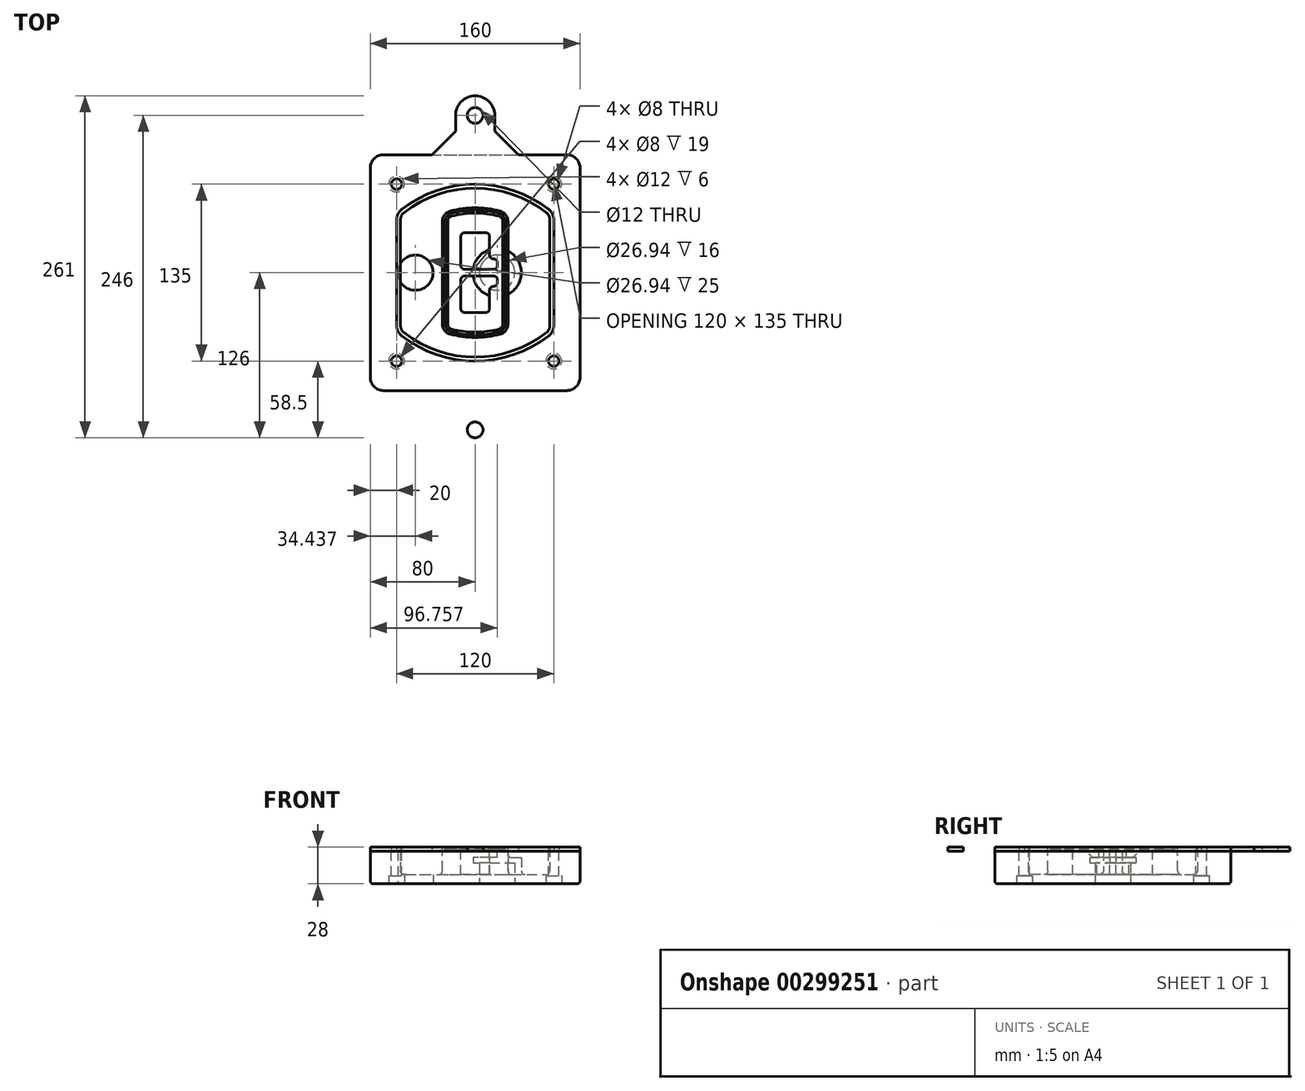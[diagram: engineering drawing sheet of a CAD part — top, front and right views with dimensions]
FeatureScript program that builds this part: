
annotation { "Feature Type Name" : "Feature", "Feature Type Description" : "" }
export const myFeature = defineFeature(function(context is Context, id is Id, definition is map)
    precondition{}
    {
        {
            var Q0;
            Q0=qCreatedBy(makeId("Top.planeOp"),FACE);
            var sketch = newSketch(context, id + "F0", { "sketchPlane" : qUnion([Q0])});
            skPoint(sketch, "E0.rect.middle", {"position": v(0, 0) * mm});
            skLineSegment(sketch, "E1.bottom", {"start": v(-70, -90) * mm, "end": v(70, -90) * mm});
            skLineSegment(sketch, "E1.top", {"start": v(-70, 90) * mm, "end": v(70, 90) * mm});
            skLineSegment(sketch, "E1.left", {"start": v(-80, -80) * mm, "end": v(-80, 80) * mm});
            skLineSegment(sketch, "E1.right", {"start": v(80, -80) * mm, "end": v(80, 80) * mm});
            skLineSegment(sketch, "E2", {"start": v(-80, 90) * mm, "end": v(80, -90) * mm, "construction": true});
            skLineSegment(sketch, "E3", {"start": v(80, 90) * mm, "end": v(-80, -90) * mm, "construction": true});
            skCircle(sketch, "E4", {"center": v(-60, 67.5) * mm, "radius": 4 * mm});
            skCircle(sketch, "E5", {"center": v(60, 67.5) * mm, "radius": 4 * mm});
            skCircle(sketch, "E6", {"center": v(60, -67.5) * mm, "radius": 4 * mm});
            skCircle(sketch, "E7", {"center": v(-60, -67.5) * mm, "radius": 4 * mm});
            skLineSegment(sketch, "E8", {"start": v(-60, 67.5) * mm, "end": v(60, 67.5) * mm, "construction": true});
            skLineSegment(sketch, "E9", {"start": v(60, 67.5) * mm, "end": v(60, -67.5) * mm, "construction": true});
            skLineSegment(sketch, "E10", {"start": v(60, -67.5) * mm, "end": v(-60, -67.5) * mm, "construction": true});
            skLineSegment(sketch, "E11", {"start": v(-60, -67.5) * mm, "end": v(-60, 67.5) * mm, "construction": true});
            skLineSegment(sketch, "E12", {"start": v(-60, 40.3) * mm, "end": v(-60, -40.3) * mm});
            skLineSegment(sketch, "E13", {"start": v(60, 40.3) * mm, "end": v(60, -40.3) * mm});
            skArc(sketch, "E14", {"start": v(56.15, 48.18) * mm, "mid": v(0, 67.5) * mm, "end": v(-56.15, 48.18) * mm});
            skArc(sketch, "E15", {"start": v(-56.15, -48.18) * mm, "mid": v(0, -67.5) * mm, "end": v(56.15, -48.18) * mm});
            skLineSegment(sketch, "E16", {"start": v(-60, 0) * mm, "end": v(60, 0) * mm, "construction": true});
            skPoint(sketch, "E17.visualSharp", {"position": v(-60, -45) * mm});
            skArc(sketch, "E17.filletArc", {"start": v(-60, -40.3) * mm, "mid": v(-58.99, -44.68) * mm, "end": v(-56.15, -48.18) * mm});
            skPoint(sketch, "E18.visualSharp", {"position": v(-60, 45) * mm});
            skArc(sketch, "E18.filletArc", {"start": v(-56.15, 48.18) * mm, "mid": v(-58.99, 44.68) * mm, "end": v(-60, 40.3) * mm});
            skPoint(sketch, "E19.visualSharp", {"position": v(60, 45) * mm});
            skArc(sketch, "E19.filletArc", {"start": v(60, 40.3) * mm, "mid": v(58.99, 44.68) * mm, "end": v(56.15, 48.18) * mm});
            skPoint(sketch, "E20.visualSharp", {"position": v(60, -45) * mm});
            skArc(sketch, "E20.filletArc", {"start": v(56.15, -48.18) * mm, "mid": v(58.99, -44.68) * mm, "end": v(60, -40.3) * mm});
            skPoint(sketch, "E21.visualSharp", {"position": v(-80, 90) * mm});
            skArc(sketch, "E21.filletArc", {"start": v(-70, 90) * mm, "mid": v(-77.07, 87.07) * mm, "end": v(-80, 80) * mm});
            skPoint(sketch, "E22.visualSharp", {"position": v(80, 90) * mm});
            skArc(sketch, "E22.filletArc", {"start": v(80, 80) * mm, "mid": v(77.07, 87.07) * mm, "end": v(70, 90) * mm});
            skPoint(sketch, "E23.visualSharp", {"position": v(80, -90) * mm});
            skArc(sketch, "E23.filletArc", {"start": v(70, -90) * mm, "mid": v(77.07, -87.07) * mm, "end": v(80, -80) * mm});
            skPoint(sketch, "E24.visualSharp", {"position": v(-80, -90) * mm});
            skArc(sketch, "E24.filletArc", {"start": v(-80, -80) * mm, "mid": v(-77.07, -87.07) * mm, "end": v(-70, -90) * mm});
            skArc(sketch, "E25.0", {"start": v(57, 40.3) * mm, "mid": v(56.3, 43.36) * mm, "end": v(54.3, 45.81) * mm});
            skLineSegment(sketch, "E25.1", {"start": v(57, 40.3) * mm, "end": v(57, -40.3) * mm});
            skArc(sketch, "E25.2", {"start": v(54.3, -45.81) * mm, "mid": v(56.3, -43.36) * mm, "end": v(57, -40.3) * mm});
            skArc(sketch, "E25.3", {"start": v(-54.3, -45.81) * mm, "mid": v(0, -64.5) * mm, "end": v(54.3, -45.81) * mm});
            skArc(sketch, "E25.4", {"start": v(-57, -40.3) * mm, "mid": v(-56.3, -43.36) * mm, "end": v(-54.3, -45.81) * mm});
            skArc(sketch, "E25.5", {"start": v(54.3, 45.81) * mm, "mid": v(0, 64.5) * mm, "end": v(-54.3, 45.81) * mm});
            skLineSegment(sketch, "E25.6", {"start": v(-57, 40.3) * mm, "end": v(-57, -40.3) * mm});
            skArc(sketch, "E25.7", {"start": v(-54.3, 45.81) * mm, "mid": v(-56.3, 43.36) * mm, "end": v(-57, 40.3) * mm});
            skArc(sketch, "E26.0", {"start": v(-58.62, 51.33) * mm, "mid": v(-62.58, 46.43) * mm, "end": v(-64, 40.3) * mm});
            skArc(sketch, "E26.1", {"start": v(58.62, 51.33) * mm, "mid": v(0, 71.5) * mm, "end": v(-58.62, 51.33) * mm});
            skArc(sketch, "E26.2", {"start": v(64, 40.3) * mm, "mid": v(62.58, 46.43) * mm, "end": v(58.62, 51.33) * mm});
            skLineSegment(sketch, "E26.3", {"start": v(64, 40.3) * mm, "end": v(64, -40.3) * mm});
            skArc(sketch, "E26.4", {"start": v(58.62, -51.33) * mm, "mid": v(62.58, -46.43) * mm, "end": v(64, -40.3) * mm});
            skLineSegment(sketch, "E26.5", {"start": v(-64, 40.3) * mm, "end": v(-64, -40.3) * mm});
            skArc(sketch, "E26.6", {"start": v(-58.62, -51.33) * mm, "mid": v(0, -71.5) * mm, "end": v(58.62, -51.33) * mm});
            skArc(sketch, "E26.7", {"start": v(-64, -40.3) * mm, "mid": v(-62.58, -46.43) * mm, "end": v(-58.62, -51.33) * mm});
            skSolve(sketch);
        }
        {
            var Q0;
            Q0=makeQuery(id+"F0.imprint","IMPRINT",FACE,{"disambiguationData":[TD([[makeQuery(id+"F0.imprint","IMPRINT",EDGE,{"derivedFrom":sQuery(id+"F0.wireOp",EDGE,"E1.bottom")}),1.0]])]});
            var Q1;
            Q1=makeQuery(id+"F0.imprint","IMPRINT",FACE,{"disambiguationData":[TD([[makeQuery(id+"F0.imprint","IMPRINT",EDGE,{"derivedFrom":sQuery(id+"F0.wireOp",EDGE,"E12")}),1.0]])]});
            var Q2;
            Q2=makeQuery(id+"F0.imprint","IMPRINT",FACE,{"disambiguationData":[TD([[makeQuery(id+"F0.imprint","IMPRINT",EDGE,{"derivedFrom":sQuery(id+"F0.wireOp",EDGE,"E25.0")}),1.0]])]});
            var Q3;
            Q3=makeQuery(id+"F0.imprint","IMPRINT",FACE,{"disambiguationData":[TD([[makeQuery(id+"F0.imprint","IMPRINT",EDGE,{"derivedFrom":sQuery(id+"F0.wireOp",EDGE,"E12")}),-1.0]])]});
            extrude(context, id + "F1", {"entities" : qUnion([Q0, Q1, Q2, Q3]), "oppositeDirection" : true, "depth" : 25 * mm});
        }
        {
            var Q0;
            Q0=makeQuery(id+"F0.imprint","IMPRINT",FACE,{"disambiguationData":[TD([[makeQuery(id+"F0.imprint","IMPRINT",EDGE,{"derivedFrom":sQuery(id+"F0.wireOp",EDGE,"E12")}),1.0]])]});
            extrude(context, id + "F2", {"entities" : qUnion([Q0]), "operationType" : NewBodyOperationType.ADD, "depth" : 3 * mm});
        }
        {
            var Q0;
            Q0=makeQuery(id+"F0.imprint","IMPRINT",FACE,{"disambiguationData":[TD([[makeQuery(id+"F0.imprint","IMPRINT",EDGE,{"derivedFrom":sQuery(id+"F0.wireOp",EDGE,"E25.0")}),1.0]])]});
            extrude(context, id + "F3", {"entities" : qUnion([Q0]), "operationType" : NewBodyOperationType.REMOVE, "oppositeDirection" : true, "depth" : 18 * mm});
        }
        {
            var Q0;
            Q0=makeQuery(id+"F2.opExtrude","CAP_FACE",FACE,{"disambiguationData":[OSD([sQuery(id+"F0.wireOp",EDGE,"E12"),sQuery(id+"F0.wireOp",EDGE,"E13"),sQuery(id+"F0.wireOp",EDGE,"E14"),sQuery(id+"F0.wireOp",EDGE,"E15"),sQuery(id+"F0.wireOp",EDGE,"E17.filletArc"),sQuery(id+"F0.wireOp",EDGE,"E18.filletArc"),sQuery(id+"F0.wireOp",EDGE,"E19.filletArc"),sQuery(id+"F0.wireOp",EDGE,"E20.filletArc"),sQuery(id+"F0.wireOp",EDGE,"E25.0"),sQuery(id+"F0.wireOp",EDGE,"E25.1"),sQuery(id+"F0.wireOp",EDGE,"E25.2"),sQuery(id+"F0.wireOp",EDGE,"E25.3"),sQuery(id+"F0.wireOp",EDGE,"E25.4"),sQuery(id+"F0.wireOp",EDGE,"E25.5"),sQuery(id+"F0.wireOp",EDGE,"E25.6"),sQuery(id+"F0.wireOp",EDGE,"E25.7")])],"isStart":false});
            var sketch = newSketch(context, id + "F4", { "sketchPlane" : qUnion([Q0])});
            skArc(sketch, "E27.0", {"start": v(-19.08, -46.97) * mm, "mid": v(0, -49.5) * mm, "end": v(19.08, -46.97) * mm});
            skArc(sketch, "E28.0", {"start": v(19.08, 46.97) * mm, "mid": v(0, 49.5) * mm, "end": v(-19.08, 46.97) * mm});
            skLineSegment(sketch, "E29", {"start": v(-25, 39.25) * mm, "end": v(-25, -39.25) * mm});
            skLineSegment(sketch, "E30", {"start": v(25, 39.25) * mm, "end": v(25, -39.25) * mm});
            skLineSegment(sketch, "E31", {"start": v(-25, 45.1) * mm, "end": v(25, 45.1) * mm, "construction": true});
            skLineSegment(sketch, "E32", {"start": v(-25, -45.1) * mm, "end": v(25, -45.1) * mm, "construction": true});
            skPoint(sketch, "E33.visualSharp", {"position": v(-25, 45.1) * mm});
            skArc(sketch, "E33.filletArc", {"start": v(-19.08, 46.97) * mm, "mid": v(-23.35, 44.11) * mm, "end": v(-25, 39.25) * mm});
            skPoint(sketch, "E34.visualSharp", {"position": v(25, 45.1) * mm});
            skArc(sketch, "E34.filletArc", {"start": v(25, 39.25) * mm, "mid": v(23.35, 44.11) * mm, "end": v(19.08, 46.97) * mm});
            skPoint(sketch, "E35.visualSharp", {"position": v(25, -45.1) * mm});
            skArc(sketch, "E35.filletArc", {"start": v(19.08, -46.97) * mm, "mid": v(23.35, -44.11) * mm, "end": v(25, -39.25) * mm});
            skPoint(sketch, "E36.visualSharp", {"position": v(-25, -45.1) * mm});
            skArc(sketch, "E36.filletArc", {"start": v(-25, -39.25) * mm, "mid": v(-23.35, -44.11) * mm, "end": v(-19.08, -46.97) * mm});
            skArc(sketch, "E37.0", {"start": v(54.3, 45.81) * mm, "mid": v(0, 64.5) * mm, "end": v(-54.3, 45.81) * mm});
            skArc(sketch, "E37.1", {"start": v(-54.3, 45.81) * mm, "mid": v(-56.3, 43.36) * mm, "end": v(-57, 40.3) * mm});
            skLineSegment(sketch, "E37.2", {"start": v(-57, 40.3) * mm, "end": v(-57, -40.3) * mm});
            skArc(sketch, "E37.3", {"start": v(-57, -40.3) * mm, "mid": v(-56.3, -43.36) * mm, "end": v(-54.3, -45.81) * mm});
            skArc(sketch, "E37.4", {"start": v(-54.3, -45.81) * mm, "mid": v(0, -64.5) * mm, "end": v(54.3, -45.81) * mm});
            skArc(sketch, "E37.5", {"start": v(54.3, -45.81) * mm, "mid": v(56.3, -43.36) * mm, "end": v(57, -40.3) * mm});
            skLineSegment(sketch, "E37.6", {"start": v(57, 40.3) * mm, "end": v(57, -40.3) * mm});
            skArc(sketch, "E37.7", {"start": v(57, 40.3) * mm, "mid": v(56.3, 43.36) * mm, "end": v(54.3, 45.81) * mm});
            skLineSegment(sketch, "E38.0", {"start": v(23, 39.25) * mm, "end": v(23, -39.25) * mm});
            skArc(sketch, "E38.1", {"start": v(18.56, -45.04) * mm, "mid": v(21.76, -42.9) * mm, "end": v(23, -39.25) * mm});
            skArc(sketch, "E38.2", {"start": v(-18.56, -45.04) * mm, "mid": v(0, -47.5) * mm, "end": v(18.56, -45.04) * mm});
            skArc(sketch, "E38.3", {"start": v(-23, -39.25) * mm, "mid": v(-21.76, -42.9) * mm, "end": v(-18.56, -45.04) * mm});
            skLineSegment(sketch, "E38.4", {"start": v(-23, 39.25) * mm, "end": v(-23, -39.25) * mm});
            skArc(sketch, "E38.5", {"start": v(23, 39.25) * mm, "mid": v(21.76, 42.9) * mm, "end": v(18.56, 45.04) * mm});
            skArc(sketch, "E38.6", {"start": v(-18.56, 45.04) * mm, "mid": v(-21.76, 42.9) * mm, "end": v(-23, 39.25) * mm});
            skArc(sketch, "E38.7", {"start": v(18.56, 45.04) * mm, "mid": v(0, 47.5) * mm, "end": v(-18.56, 45.04) * mm});
            skArc(sketch, "E39.0", {"start": v(21, 39.25) * mm, "mid": v(20.18, 41.68) * mm, "end": v(18.04, 43.1) * mm});
            skLineSegment(sketch, "E39.1", {"start": v(21, 39.25) * mm, "end": v(21, -39.25) * mm});
            skArc(sketch, "E39.2", {"start": v(18.04, -43.1) * mm, "mid": v(20.18, -41.68) * mm, "end": v(21, -39.25) * mm});
            skArc(sketch, "E39.3", {"start": v(-18.04, -43.1) * mm, "mid": v(0, -45.5) * mm, "end": v(18.04, -43.1) * mm});
            skArc(sketch, "E39.4", {"start": v(-21, -39.25) * mm, "mid": v(-20.18, -41.68) * mm, "end": v(-18.04, -43.1) * mm});
            skArc(sketch, "E39.5", {"start": v(18.04, 43.1) * mm, "mid": v(0, 45.5) * mm, "end": v(-18.04, 43.1) * mm});
            skLineSegment(sketch, "E39.6", {"start": v(-21, 39.25) * mm, "end": v(-21, -39.25) * mm});
            skArc(sketch, "E39.7", {"start": v(-18.04, 43.1) * mm, "mid": v(-20.18, 41.68) * mm, "end": v(-21, 39.25) * mm});
            skLineSegment(sketch, "E40", {"start": v(-25, 0) * mm, "end": v(25, 0) * mm, "construction": true});
            skLineSegment(sketch, "E41", {"start": v(-11, 5.5) * mm, "end": v(-11, 27.5) * mm});
            skLineSegment(sketch, "E42", {"start": v(-8, 30.5) * mm, "end": v(8, 30.5) * mm});
            skLineSegment(sketch, "E43", {"start": v(11, 27.5) * mm, "end": v(11, 13.5) * mm});
            skLineSegment(sketch, "E44", {"start": v(14, 10.5) * mm, "end": v(14, 10.5) * mm});
            skLineSegment(sketch, "E45", {"start": v(17, 7.5) * mm, "end": v(17, 5.5) * mm});
            skLineSegment(sketch, "E46", {"start": v(14, 2.5) * mm, "end": v(-8, 2.5) * mm});
            skPoint(sketch, "E47.visualSharp", {"position": v(-11, 30.5) * mm});
            skArc(sketch, "E47.filletArc", {"start": v(-8, 30.5) * mm, "mid": v(-10.12, 29.62) * mm, "end": v(-11, 27.5) * mm});
            skPoint(sketch, "E48.visualSharp", {"position": v(11, 30.5) * mm});
            skArc(sketch, "E48.filletArc", {"start": v(11, 27.5) * mm, "mid": v(10.12, 29.62) * mm, "end": v(8, 30.5) * mm});
            skPoint(sketch, "E49.visualSharp", {"position": v(11, 10.5) * mm});
            skArc(sketch, "E49.filletArc", {"start": v(11, 13.5) * mm, "mid": v(11.88, 11.38) * mm, "end": v(14, 10.5) * mm});
            skPoint(sketch, "E50.visualSharp", {"position": v(17, 10.5) * mm});
            skArc(sketch, "E50.filletArc", {"start": v(17, 7.5) * mm, "mid": v(16.12, 9.62) * mm, "end": v(14, 10.5) * mm});
            skPoint(sketch, "E51.visualSharp", {"position": v(17, 2.5) * mm});
            skArc(sketch, "E51.filletArc", {"start": v(14, 2.5) * mm, "mid": v(16.12, 3.38) * mm, "end": v(17, 5.5) * mm});
            skPoint(sketch, "E52.visualSharp", {"position": v(-11, 2.5) * mm});
            skArc(sketch, "E52.filletArc", {"start": v(-11, 5.5) * mm, "mid": v(-10.12, 3.38) * mm, "end": v(-8, 2.5) * mm});
            skLineSegment(sketch, "E53.0.MirrorCS", {"start": v(14, -2.5) * mm, "end": v(-8, -2.5) * mm});
            skArc(sketch, "E54.0.MirrorCS", {"start": v(-11, -5.5) * mm, "mid": v(-10.12, -3.38) * mm, "end": v(-8, -2.5) * mm});
            skLineSegment(sketch, "E55.0.MirrorCS", {"start": v(-11, -5.5) * mm, "end": v(-11, -27.5) * mm});
            skArc(sketch, "E56.0.MirrorCS", {"start": v(-8, -30.5) * mm, "mid": v(-10.12, -29.62) * mm, "end": v(-11, -27.5) * mm});
            skLineSegment(sketch, "E57.0.MirrorCS", {"start": v(-8, -30.5) * mm, "end": v(8, -30.5) * mm});
            skArc(sketch, "E58.0.MirrorCS", {"start": v(11, -27.5) * mm, "mid": v(10.12, -29.62) * mm, "end": v(8, -30.5) * mm});
            skLineSegment(sketch, "E59.0.MirrorCS", {"start": v(11, -27.5) * mm, "end": v(11, -13.5) * mm});
            skArc(sketch, "E60.0.MirrorCS", {"start": v(11, -13.5) * mm, "mid": v(11.88, -11.38) * mm, "end": v(14, -10.5) * mm});
            skArc(sketch, "E61.0.MirrorCS", {"start": v(17, -7.5) * mm, "mid": v(16.12, -9.62) * mm, "end": v(14, -10.5) * mm});
            skLineSegment(sketch, "E62.0.MirrorCS", {"start": v(17, -7.5) * mm, "end": v(17, -5.5) * mm});
            skArc(sketch, "E63.0.MirrorCS", {"start": v(14, -2.5) * mm, "mid": v(16.12, -3.38) * mm, "end": v(17, -5.5) * mm});
            skSolve(sketch);
        }
        {
            var Q0;
            Q0=makeQuery(id+"F4.imprint","IMPRINT",FACE,{"disambiguationData":[TD([[makeQuery(id+"F4.imprint","IMPRINT",EDGE,{"derivedFrom":sQuery(id+"F4.wireOp",EDGE,"E27.0")}),1.0]])]});
            var Q1;
            Q1=makeQuery(id+"F4.imprint","IMPRINT",FACE,{"disambiguationData":[TD([[makeQuery(id+"F4.imprint","IMPRINT",EDGE,{"derivedFrom":sQuery(id+"F4.wireOp",EDGE,"E38.0")}),-1.0]])]});
            var Q2;
            Q2=makeQuery(id+"F4.imprint","IMPRINT",FACE,{"disambiguationData":[TD([[makeQuery(id+"F4.imprint","IMPRINT",EDGE,{"derivedFrom":sQuery(id+"F4.wireOp",EDGE,"E39.0")}),1.0]])]});
            extrude(context, id + "F5", {"entities" : qUnion([Q0, Q1, Q2]), "operationType" : NewBodyOperationType.ADD, "endBound" : BoundingType.UP_TO_NEXT, "oppositeDirection" : true, "depth" : 25 * mm});
        }
        {
            var Q0;
            Q0=makeQuery(id+"F4.imprint","IMPRINT",FACE,{"disambiguationData":[TD([[makeQuery(id+"F4.imprint","IMPRINT",EDGE,{"derivedFrom":sQuery(id+"F4.wireOp",EDGE,"E38.0")}),-1.0]])]});
            extrude(context, id + "F6", {"entities" : qUnion([Q0]), "operationType" : NewBodyOperationType.REMOVE, "oppositeDirection" : true, "depth" : 2 * mm});
        }
        {
            var Q0;
            Q0=makeQuery(id+"F1.opExtrude","CAP_FACE",FACE,{"disambiguationData":[OSD([sQuery(id+"F0.wireOp",EDGE,"E1.bottom"),sQuery(id+"F0.wireOp",EDGE,"E1.top"),sQuery(id+"F0.wireOp",EDGE,"E1.left"),sQuery(id+"F0.wireOp",EDGE,"E1.right"),sQuery(id+"F0.wireOp",EDGE,"E4"),sQuery(id+"F0.wireOp",EDGE,"E5"),sQuery(id+"F0.wireOp",EDGE,"E6"),sQuery(id+"F0.wireOp",EDGE,"E7"),sQuery(id+"F0.wireOp",EDGE,"E21.filletArc"),sQuery(id+"F0.wireOp",EDGE,"E22.filletArc"),sQuery(id+"F0.wireOp",EDGE,"E23.filletArc"),sQuery(id+"F0.wireOp",EDGE,"E24.filletArc")])],"isStart":false});
            var sketch = newSketch(context, id + "F7", { "sketchPlane" : qUnion([Q0])});
            skCircle(sketch, "E64", {"center": v(16.76, 0) * mm, "radius": 13.47 * mm});
            skCircle(sketch, "E65", {"center": v(-45.56, 0) * mm, "radius": 13.47 * mm});
            skLineSegment(sketch, "E66", {"start": v(80, 0) * mm, "end": v(-80, 0) * mm});
            skCircle(sketch, "E67", {"center": v(16.76, 0) * mm, "radius": 18.47 * mm});
            skCircle(sketch, "E68", {"center": v(60, -67.5) * mm, "radius": 6 * mm});
            skCircle(sketch, "E69", {"center": v(-60, -67.5) * mm, "radius": 6 * mm});
            skCircle(sketch, "E70", {"center": v(-60, 67.5) * mm, "radius": 6 * mm});
            skCircle(sketch, "E71", {"center": v(60, 67.5) * mm, "radius": 6 * mm});
            skSolve(sketch);
        }
        {
            var Q0;
            {var subQ1=sQuery(id+"F7.wireOp",EDGE,"E66");var subQ4=sQuery(id+"F7.wireOp",EDGE,"E64");var subQ6=makeQuery(id+"F7.imprint","INTERSECT",VERTEX,{"disambiguationData":[OD(0.0)],"derivedFrom":[subQ4,subQ1]});Q0=makeQuery(id+"F7.imprint","IMPRINT",FACE,{"disambiguationData":[TD([[makeQuery(id+"F7.imprint","IMPRINT",EDGE,{"disambiguationData":[TD([[subQ6,-1.0]])],"derivedFrom":subQ4}),-1.0]])]});}
            var Q1;
            {var subQ0=sQuery(id+"F7.wireOp",EDGE,"E66");var subQ1=sQuery(id+"F7.wireOp",EDGE,"E64");var subQ3=makeQuery(id+"F7.imprint","INTERSECT",VERTEX,{"disambiguationData":[OD(0.0)],"derivedFrom":[subQ1,subQ0]});Q1=makeQuery(id+"F7.imprint","IMPRINT",FACE,{"disambiguationData":[TD([[makeQuery(id+"F7.imprint","IMPRINT",EDGE,{"disambiguationData":[TD([[subQ3,-1.0]])],"derivedFrom":subQ1}),1.0]])]});}
            var Q2;
            {var subQ0=sQuery(id+"F7.wireOp",EDGE,"E66");var subQ1=sQuery(id+"F7.wireOp",EDGE,"E64");var subQ3=makeQuery(id+"F7.imprint","INTERSECT",VERTEX,{"disambiguationData":[OD(0.0)],"derivedFrom":[subQ1,subQ0]});Q2=makeQuery(id+"F7.imprint","IMPRINT",FACE,{"disambiguationData":[TD([[makeQuery(id+"F7.imprint","IMPRINT",EDGE,{"disambiguationData":[TD([[subQ3,1.0]])],"derivedFrom":subQ1}),1.0]])]});}
            var Q3;
            {var subQ1=sQuery(id+"F7.wireOp",EDGE,"E66");var subQ4=sQuery(id+"F7.wireOp",EDGE,"E64");var subQ6=makeQuery(id+"F7.imprint","INTERSECT",VERTEX,{"disambiguationData":[OD(0.0)],"derivedFrom":[subQ4,subQ1]});Q3=makeQuery(id+"F7.imprint","IMPRINT",FACE,{"disambiguationData":[TD([[makeQuery(id+"F7.imprint","IMPRINT",EDGE,{"disambiguationData":[TD([[subQ6,1.0]])],"derivedFrom":subQ4}),-1.0]])]});}
            extrude(context, id + "F8", {"entities" : qUnion([Q0, Q1, Q2, Q3]), "operationType" : NewBodyOperationType.ADD, "oppositeDirection" : true, "depth" : 20 * mm});
        }
        {
            var Q0;
            {var subQ0=sQuery(id+"F7.wireOp",EDGE,"E66");var subQ1=sQuery(id+"F7.wireOp",EDGE,"E64");var subQ3=makeQuery(id+"F7.imprint","INTERSECT",VERTEX,{"disambiguationData":[OD(0.0)],"derivedFrom":[subQ1,subQ0]});Q0=makeQuery(id+"F7.imprint","IMPRINT",FACE,{"disambiguationData":[TD([[makeQuery(id+"F7.imprint","IMPRINT",EDGE,{"disambiguationData":[TD([[subQ3,-1.0]])],"derivedFrom":subQ1}),1.0]])]});}
            var Q1;
            {var subQ0=sQuery(id+"F7.wireOp",EDGE,"E66");var subQ1=sQuery(id+"F7.wireOp",EDGE,"E64");var subQ3=makeQuery(id+"F7.imprint","INTERSECT",VERTEX,{"disambiguationData":[OD(0.0)],"derivedFrom":[subQ1,subQ0]});Q1=makeQuery(id+"F7.imprint","IMPRINT",FACE,{"disambiguationData":[TD([[makeQuery(id+"F7.imprint","IMPRINT",EDGE,{"disambiguationData":[TD([[subQ3,1.0]])],"derivedFrom":subQ1}),1.0]])]});}
            extrude(context, id + "F9", {"entities" : qUnion([Q0, Q1]), "operationType" : NewBodyOperationType.REMOVE, "oppositeDirection" : true, "depth" : 16 * mm});
        }
        {
            var Q0;
            {var subQ0=sQuery(id+"F7.wireOp",EDGE,"E66");var subQ1=sQuery(id+"F7.wireOp",EDGE,"E65");var subQ3=makeQuery(id+"F7.imprint","INTERSECT",VERTEX,{"disambiguationData":[OD(0.0)],"derivedFrom":[subQ1,subQ0]});Q0=makeQuery(id+"F7.imprint","IMPRINT",FACE,{"disambiguationData":[TD([[makeQuery(id+"F7.imprint","IMPRINT",EDGE,{"disambiguationData":[TD([[subQ3,-1.0]])],"derivedFrom":subQ1}),1.0]])]});}
            var Q1;
            {var subQ0=sQuery(id+"F7.wireOp",EDGE,"E66");var subQ1=sQuery(id+"F7.wireOp",EDGE,"E65");var subQ3=makeQuery(id+"F7.imprint","INTERSECT",VERTEX,{"disambiguationData":[OD(0.0)],"derivedFrom":[subQ1,subQ0]});Q1=makeQuery(id+"F7.imprint","IMPRINT",FACE,{"disambiguationData":[TD([[makeQuery(id+"F7.imprint","IMPRINT",EDGE,{"disambiguationData":[TD([[subQ3,1.0]])],"derivedFrom":subQ1}),1.0]])]});}
            extrude(context, id + "F10", {"entities" : qUnion([Q0, Q1]), "operationType" : NewBodyOperationType.REMOVE, "oppositeDirection" : true, "depth" : 25 * mm});
        }
        {
            var Q0;
            Q0=makeQuery(id+"F7.imprint","IMPRINT",FACE,{"disambiguationData":[TD([[makeQuery(id+"F7.imprint","IMPRINT",EDGE,{"derivedFrom":sQuery(id+"F7.wireOp",EDGE,"E68")}),1.0]])]});
            var Q1;
            Q1=makeQuery(id+"F7.imprint","IMPRINT",FACE,{"disambiguationData":[TD([[makeQuery(id+"F7.imprint","IMPRINT",EDGE,{"derivedFrom":makeQuery(id+"F1.opExtrude","CAP_EDGE",EDGE,{"disambiguationData":[OSD([sQuery(id+"F0.wireOp",EDGE,"E5")])],"isStart":false})}),-1.0]])]});
            var Q2;
            Q2=makeQuery(id+"F7.imprint","IMPRINT",FACE,{"disambiguationData":[TD([[makeQuery(id+"F7.imprint","IMPRINT",EDGE,{"derivedFrom":sQuery(id+"F7.wireOp",EDGE,"E69")}),1.0]])]});
            var Q3;
            Q3=makeQuery(id+"F7.imprint","IMPRINT",FACE,{"disambiguationData":[TD([[makeQuery(id+"F7.imprint","IMPRINT",EDGE,{"derivedFrom":makeQuery(id+"F1.opExtrude","CAP_EDGE",EDGE,{"disambiguationData":[OSD([sQuery(id+"F0.wireOp",EDGE,"E4")])],"isStart":false})}),-1.0]])]});
            var Q4;
            Q4=makeQuery(id+"F7.imprint","IMPRINT",FACE,{"disambiguationData":[TD([[makeQuery(id+"F7.imprint","IMPRINT",EDGE,{"derivedFrom":sQuery(id+"F7.wireOp",EDGE,"E70")}),1.0]])]});
            var Q5;
            Q5=makeQuery(id+"F7.imprint","IMPRINT",FACE,{"disambiguationData":[TD([[makeQuery(id+"F7.imprint","IMPRINT",EDGE,{"derivedFrom":makeQuery(id+"F1.opExtrude","CAP_EDGE",EDGE,{"disambiguationData":[OSD([sQuery(id+"F0.wireOp",EDGE,"E7")])],"isStart":false})}),-1.0]])]});
            var Q6;
            Q6=makeQuery(id+"F7.imprint","IMPRINT",FACE,{"disambiguationData":[TD([[makeQuery(id+"F7.imprint","IMPRINT",EDGE,{"derivedFrom":sQuery(id+"F7.wireOp",EDGE,"E71")}),1.0]])]});
            var Q7;
            Q7=makeQuery(id+"F7.imprint","IMPRINT",FACE,{"disambiguationData":[TD([[makeQuery(id+"F7.imprint","IMPRINT",EDGE,{"derivedFrom":makeQuery(id+"F1.opExtrude","CAP_EDGE",EDGE,{"disambiguationData":[OSD([sQuery(id+"F0.wireOp",EDGE,"E6")])],"isStart":false})}),-1.0]])]});
            extrude(context, id + "F11", {"entities" : qUnion([Q0, Q1, Q2, Q3, Q4, Q5, Q6, Q7]), "operationType" : NewBodyOperationType.REMOVE, "oppositeDirection" : true, "depth" : 6 * mm});
        }
        {
            var Q0;
            Q0=makeQuery(id+"F9.boolean.opBoolean","COPY",FACE,{"derivedFrom":makeQuery(id+"F9.opExtrude","CAP_FACE",FACE,{"disambiguationData":[OSD([sQuery(id+"F7.wireOp",EDGE,"E64")])],"isStart":false})});
            var sketch = newSketch(context, id + "F12", { "sketchPlane" : qUnion([Q0])});
            skArc(sketch, "E72.0", {"start": v(11, 17.55) * mm, "mid": v(2.57, 11.82) * mm, "end": v(-1.54, 2.5) * mm});
            skArc(sketch, "E72.1", {"start": v(-1.54, -2.5) * mm, "mid": v(2.57, -11.82) * mm, "end": v(11, -17.55) * mm});
            skLineSegment(sketch, "E73", {"start": v(-1.54, -2.5) * mm, "end": v(14, -2.5) * mm});
            skLineSegment(sketch, "E74.0", {"start": v(14, 2.5) * mm, "end": v(-1.54, 2.5) * mm});
            skArc(sketch, "E74.1", {"start": v(14, 2.5) * mm, "mid": v(16.12, 3.38) * mm, "end": v(17, 5.5) * mm});
            skLineSegment(sketch, "E74.2", {"start": v(17, 7.5) * mm, "end": v(17, 5.5) * mm});
            skArc(sketch, "E74.3", {"start": v(17, 7.5) * mm, "mid": v(16.12, 9.62) * mm, "end": v(14, 10.5) * mm});
            skArc(sketch, "E74.4", {"start": v(11, 13.5) * mm, "mid": v(11.88, 11.38) * mm, "end": v(14, 10.5) * mm});
            skLineSegment(sketch, "E74.5", {"start": v(11, 17.55) * mm, "end": v(11, 13.5) * mm});
            skLineSegment(sketch, "E74.7", {"start": v(14, -2.5) * mm, "end": v(-1.54, -2.5) * mm});
            skArc(sketch, "E74.8", {"start": v(14, -2.5) * mm, "mid": v(16.12, -3.38) * mm, "end": v(17, -5.5) * mm});
            skLineSegment(sketch, "E74.9", {"start": v(17, -7.5) * mm, "end": v(17, -5.5) * mm});
            skArc(sketch, "E74.10", {"start": v(17, -7.5) * mm, "mid": v(16.12, -9.62) * mm, "end": v(14, -10.5) * mm});
            skArc(sketch, "E74.11", {"start": v(11, -13.5) * mm, "mid": v(11.88, -11.38) * mm, "end": v(14, -10.5) * mm});
            skLineSegment(sketch, "E74.12", {"start": v(11, -17.55) * mm, "end": v(11, -13.5) * mm});
            skPoint(sketch, "E75.orphan", {"position": v(11, -27.5) * mm});
            skPoint(sketch, "E76.orphan", {"position": v(-8, -2.5) * mm});
            skPoint(sketch, "E77.orphan", {"position": v(-8, 2.5) * mm});
            skPoint(sketch, "E78.orphan", {"position": v(11, 27.5) * mm});
            skSolve(sketch);
        }
        {
            var Q0;
            {var subQ7=sQuery(id+"F12.wireOp",EDGE,"E72.0");var subQ14=sQuery(id+"F12.wireOp",EDGE,"E72.1");var subQ16=sQuery(id+"F12.wireOp",EDGE,"E74.1");var subQ18=sQuery(id+"F12.wireOp",EDGE,"E74.8");Q0=qUnion([makeQuery(id+"F12.imprint","IMPRINT",FACE,{"disambiguationData":[TD([[makeQuery(id+"F12.imprint","IMPRINT",EDGE,{"derivedFrom":subQ7}),1.0]])]}),makeQuery(id+"F12.imprint","IMPRINT",FACE,{"disambiguationData":[TD([[makeQuery(id+"F12.imprint","IMPRINT",EDGE,{"derivedFrom":subQ14}),1.0]])]}),makeQuery(id+"F12.imprint","IMPRINT",FACE,{"disambiguationData":[TD([[makeQuery(id+"F12.imprint","IMPRINT",EDGE,{"derivedFrom":subQ16}),1.0]])]}),makeQuery(id+"F12.imprint","IMPRINT",FACE,{"disambiguationData":[TD([[makeQuery(id+"F12.imprint","IMPRINT",EDGE,{"derivedFrom":subQ18}),-1.0]])]})]);}
            var Q1;
            Q1=makeQuery(id+"F5.boolean.opBoolean","SPLIT",FACE,{"disambiguationData":[TD([makeQuery(id+"F5.opExtrude","SWEPT_FACE",FACE,{"disambiguationData":[OSD([sQuery(id+"F4.wireOp",EDGE,"E41")])]})])],"derivedFrom":makeQuery(id+"F3.boolean.opBoolean","COPY",FACE,{"derivedFrom":makeQuery(id+"F3.opExtrude","CAP_FACE",FACE,{"disambiguationData":[OSD([sQuery(id+"F0.wireOp",EDGE,"E25.0"),sQuery(id+"F0.wireOp",EDGE,"E25.1"),sQuery(id+"F0.wireOp",EDGE,"E25.2"),sQuery(id+"F0.wireOp",EDGE,"E25.3"),sQuery(id+"F0.wireOp",EDGE,"E25.4"),sQuery(id+"F0.wireOp",EDGE,"E25.5"),sQuery(id+"F0.wireOp",EDGE,"E25.6"),sQuery(id+"F0.wireOp",EDGE,"E25.7")])],"isStart":false})})});
            extrude(context, id + "F13", {"entities" : qUnion([Q0]), "operationType" : NewBodyOperationType.REMOVE, "endBound" : BoundingType.UP_TO_SURFACE, "endBoundEntityFace" : qUnion([Q1]), "depth" : 25 * mm});
        }
        {
            var Q0;
            Q0=makeQuery(id+"F3.boolean.opBoolean","COPY",EDGE,{"derivedFrom":makeQuery(id+"F3.opExtrude","CAP_EDGE",EDGE,{"disambiguationData":[OSD([sQuery(id+"F0.wireOp",EDGE,"E25.6")])],"isStart":false})});
            var Q1;
            Q1=makeQuery(id+"F8.boolean.opBoolean","INTERSECT",EDGE,{"derivedFrom":[makeQuery(id+"F5.opExtrude","SWEPT_FACE",FACE,{"disambiguationData":[OSD([sQuery(id+"F4.wireOp",EDGE,"E30")])]}),makeQuery(id+"F8.opExtrude","CAP_FACE",FACE,{"disambiguationData":[OSD([sQuery(id+"F7.wireOp",EDGE,"E67")])],"isStart":false})]});
            var Q2;
            Q2=makeQuery(id+"F8.boolean.opBoolean","INTERSECT",EDGE,{"disambiguationData":[OD(1.0)],"derivedFrom":[makeQuery(id+"F5.opExtrude","SWEPT_FACE",FACE,{"disambiguationData":[OSD([sQuery(id+"F4.wireOp",EDGE,"E30")])]}),makeQuery(id+"F8.opExtrude","SWEPT_FACE",FACE,{"disambiguationData":[OSD([sQuery(id+"F7.wireOp",EDGE,"E67")])]})]});
            var Q3;
            {var subQ0=sQuery(id+"F4.wireOp",EDGE,"E30");Q3=makeQuery(id+"F8.boolean.opBoolean","SPLIT",EDGE,{"disambiguationData":[TD([makeQuery(id+"F5.opExtrude","SWEPT_FACE",FACE,{"disambiguationData":[OSD([sQuery(id+"F4.wireOp",EDGE,"E35.filletArc")])]})])],"derivedFrom":makeQuery(id+"F5.opExtrude","CAP_EDGE",EDGE,{"disambiguationData":[OSD([subQ0])],"isStart":false})});}
            var Q4;
            {var subQ0=sQuery(id+"F0.wireOp",EDGE,"E25.7");var subQ1=sQuery(id+"F0.wireOp",EDGE,"E25.1");var subQ2=sQuery(id+"F0.wireOp",EDGE,"E25.6");var subQ3=sQuery(id+"F0.wireOp",EDGE,"E25.5");var subQ4=sQuery(id+"F0.wireOp",EDGE,"E25.4");var subQ5=sQuery(id+"F0.wireOp",EDGE,"E25.0");var subQ6=sQuery(id+"F0.wireOp",EDGE,"E25.2");var subQ7=sQuery(id+"F0.wireOp",EDGE,"E25.3");Q4=makeQuery(id+"F8.boolean.opBoolean","INTERSECT",EDGE,{"derivedFrom":[makeQuery(id+"F5.boolean.opBoolean","SPLIT",FACE,{"disambiguationData":[TD([makeQuery(id+"F2.opExtrude","SWEPT_FACE",FACE,{"disambiguationData":[OSD([subQ5])]})])],"derivedFrom":makeQuery(id+"F3.boolean.opBoolean","COPY",FACE,{"derivedFrom":makeQuery(id+"F3.opExtrude","CAP_FACE",FACE,{"disambiguationData":[OSD([subQ5,subQ1,subQ6,subQ7,subQ4,subQ3,subQ2,subQ0])],"isStart":false})})}),makeQuery(id+"F8.opExtrude","SWEPT_FACE",FACE,{"disambiguationData":[OSD([sQuery(id+"F7.wireOp",EDGE,"E67")])]})]});}
            var Q5;
            Q5=makeQuery(id+"F8.boolean.opBoolean","INTERSECT",EDGE,{"disambiguationData":[OD(0.0)],"derivedFrom":[makeQuery(id+"F5.opExtrude","SWEPT_FACE",FACE,{"disambiguationData":[OSD([sQuery(id+"F4.wireOp",EDGE,"E30")])]}),makeQuery(id+"F8.opExtrude","SWEPT_FACE",FACE,{"disambiguationData":[OSD([sQuery(id+"F7.wireOp",EDGE,"E67")])]})]});
            fillet(context, id + "F14", {"entities" : qUnion([Q0, Q1, Q2, Q3, Q4, Q5]), "radius" : 3 * mm, "tangentPropagation" : true, "allowEdgeOverflow" : false});
        }
        {
            var Q0;
            Q0=makeQuery(id+"F1.opExtrude","CAP_EDGE",EDGE,{"disambiguationData":[OSD([sQuery(id+"F0.wireOp",EDGE,"E1.bottom")])],"isStart":false});
            fillet(context, id + "F15", {"entities" : qUnion([Q0]), "radius" : 2 * mm, "tangentPropagation" : true, "allowEdgeOverflow" : false});
        }
        {
            var Q0;
            {var subQ0=sQuery(id+"F0.wireOp",EDGE,"E21.filletArc");var subQ1=sQuery(id+"F0.wireOp",EDGE,"E7");var subQ2=sQuery(id+"F0.wireOp",EDGE,"E6");var subQ3=sQuery(id+"F0.wireOp",EDGE,"E5");var subQ4=sQuery(id+"F0.wireOp",EDGE,"E4");var subQ5=sQuery(id+"F0.wireOp",EDGE,"E22.filletArc");var subQ6=sQuery(id+"F0.wireOp",EDGE,"E1.bottom");var subQ7=sQuery(id+"F0.wireOp",EDGE,"E1.right");var subQ8=sQuery(id+"F0.wireOp",EDGE,"E1.top");var subQ9=sQuery(id+"F0.wireOp",EDGE,"E1.left");var subQ10=sQuery(id+"F0.wireOp",EDGE,"E23.filletArc");var subQ11=sQuery(id+"F0.wireOp",EDGE,"E24.filletArc");Q0=makeQuery(id+"F2.boolean.opBoolean","SPLIT",FACE,{"disambiguationData":[TD([makeQuery(id+"F1.opExtrude","SWEPT_FACE",FACE,{"disambiguationData":[OSD([subQ6])]})])],"derivedFrom":makeQuery(id+"F1.opExtrude","CAP_FACE",FACE,{"disambiguationData":[OSD([subQ6,subQ8,subQ9,subQ7,subQ4,subQ3,subQ2,subQ1,subQ0,subQ5,subQ10,subQ11])],"isStart":true})});}
            var sketch = newSketch(context, id + "F16", { "sketchPlane" : qUnion([Q0])});
            skLineSegment(sketch, "E79", {"start": v(0, 90) * mm, "end": v(0, 120) * mm, "construction": true});
            skCircle(sketch, "E80", {"center": v(0, 120) * mm, "radius": 6 * mm});
            skArc(sketch, "E81", {"start": v(15, 120) * mm, "mid": v(0, 135) * mm, "end": v(-15, 120) * mm});
            skLineSegment(sketch, "E82", {"start": v(-15, 120) * mm, "end": v(-15, 108) * mm});
            skLineSegment(sketch, "E83", {"start": v(-15, 108) * mm, "end": v(-33, 90) * mm});
            skLineSegment(sketch, "E84", {"start": v(15, 120) * mm, "end": v(15, 108) * mm});
            skLineSegment(sketch, "E85", {"start": v(15, 108) * mm, "end": v(33, 90) * mm});
            skLineSegment(sketch, "E86", {"start": v(-80, 0) * mm, "end": v(80, 0) * mm, "construction": true});
            skLineSegment(sketch, "E87.MirrorCS", {"start": v(15, -108) * mm, "end": v(33, -90) * mm});
            skCircle(sketch, "E88.MirrorC", {"center": v(0, -120) * mm, "radius": 6 * mm});
            skLineSegment(sketch, "E89.MirrorCS", {"start": v(0, -90) * mm, "end": v(0, -120) * mm, "construction": true});
            skLineSegment(sketch, "E90.MirrorCS", {"start": v(15, -120) * mm, "end": v(15, -108) * mm});
            skLineSegment(sketch, "E91.MirrorCS", {"start": v(-15, -108) * mm, "end": v(-33, -90) * mm});
            skLineSegment(sketch, "E92.MirrorCS", {"start": v(-15, -120) * mm, "end": v(-15, -108) * mm});
            skArc(sketch, "E93.MirrorCS", {"start": v(15, -120) * mm, "mid": v(0, -135) * mm, "end": v(-15, -120) * mm});
            skSolve(sketch);
        }
        {
            var Q0;
            Q0=makeQuery(id+"F16.imprint","IMPRINT",FACE,{"disambiguationData":[TD([[makeQuery(id+"F16.imprint","IMPRINT",EDGE,{"derivedFrom":sQuery(id+"F16.wireOp",EDGE,"E80")}),-1.0]])]});
            var Q1;
            Q1=makeQuery(id+"F16.imprint","IMPRINT",FACE,{"disambiguationData":[TD([[makeQuery(id+"F16.imprint","IMPRINT",EDGE,{"derivedFrom":makeQuery(id+"F1.opExtrude","CAP_EDGE",EDGE,{"disambiguationData":[OSD([sQuery(id+"F0.wireOp",EDGE,"E1.left")])],"isStart":true})}),-1.0]])]});
            var Q2;
            Q2=makeQuery(id+"F16.imprint","IMPRINT",FACE,{"disambiguationData":[TD([[makeQuery(id+"F16.imprint","IMPRINT",EDGE,{"derivedFrom":sQuery(id+"F16.wireOp",EDGE,"E88.MirrorC")}),1.0]])]});
            var Q3;
            Q3=makeQuery(id+"F2.opExtrude","CAP_FACE",FACE,{"disambiguationData":[OSD([sQuery(id+"F0.wireOp",EDGE,"E12"),sQuery(id+"F0.wireOp",EDGE,"E13"),sQuery(id+"F0.wireOp",EDGE,"E14"),sQuery(id+"F0.wireOp",EDGE,"E15"),sQuery(id+"F0.wireOp",EDGE,"E17.filletArc"),sQuery(id+"F0.wireOp",EDGE,"E18.filletArc"),sQuery(id+"F0.wireOp",EDGE,"E19.filletArc"),sQuery(id+"F0.wireOp",EDGE,"E20.filletArc"),sQuery(id+"F0.wireOp",EDGE,"E25.0"),sQuery(id+"F0.wireOp",EDGE,"E25.1"),sQuery(id+"F0.wireOp",EDGE,"E25.2"),sQuery(id+"F0.wireOp",EDGE,"E25.3"),sQuery(id+"F0.wireOp",EDGE,"E25.4"),sQuery(id+"F0.wireOp",EDGE,"E25.5"),sQuery(id+"F0.wireOp",EDGE,"E25.6"),sQuery(id+"F0.wireOp",EDGE,"E25.7")])],"isStart":false});
            extrude(context, id + "F17", {"entities" : qUnion([Q0, Q1, Q2]), "endBound" : BoundingType.UP_TO_SURFACE, "endBoundEntityFace" : qUnion([Q3]), "depth" : 25 * mm});
        }
    });
